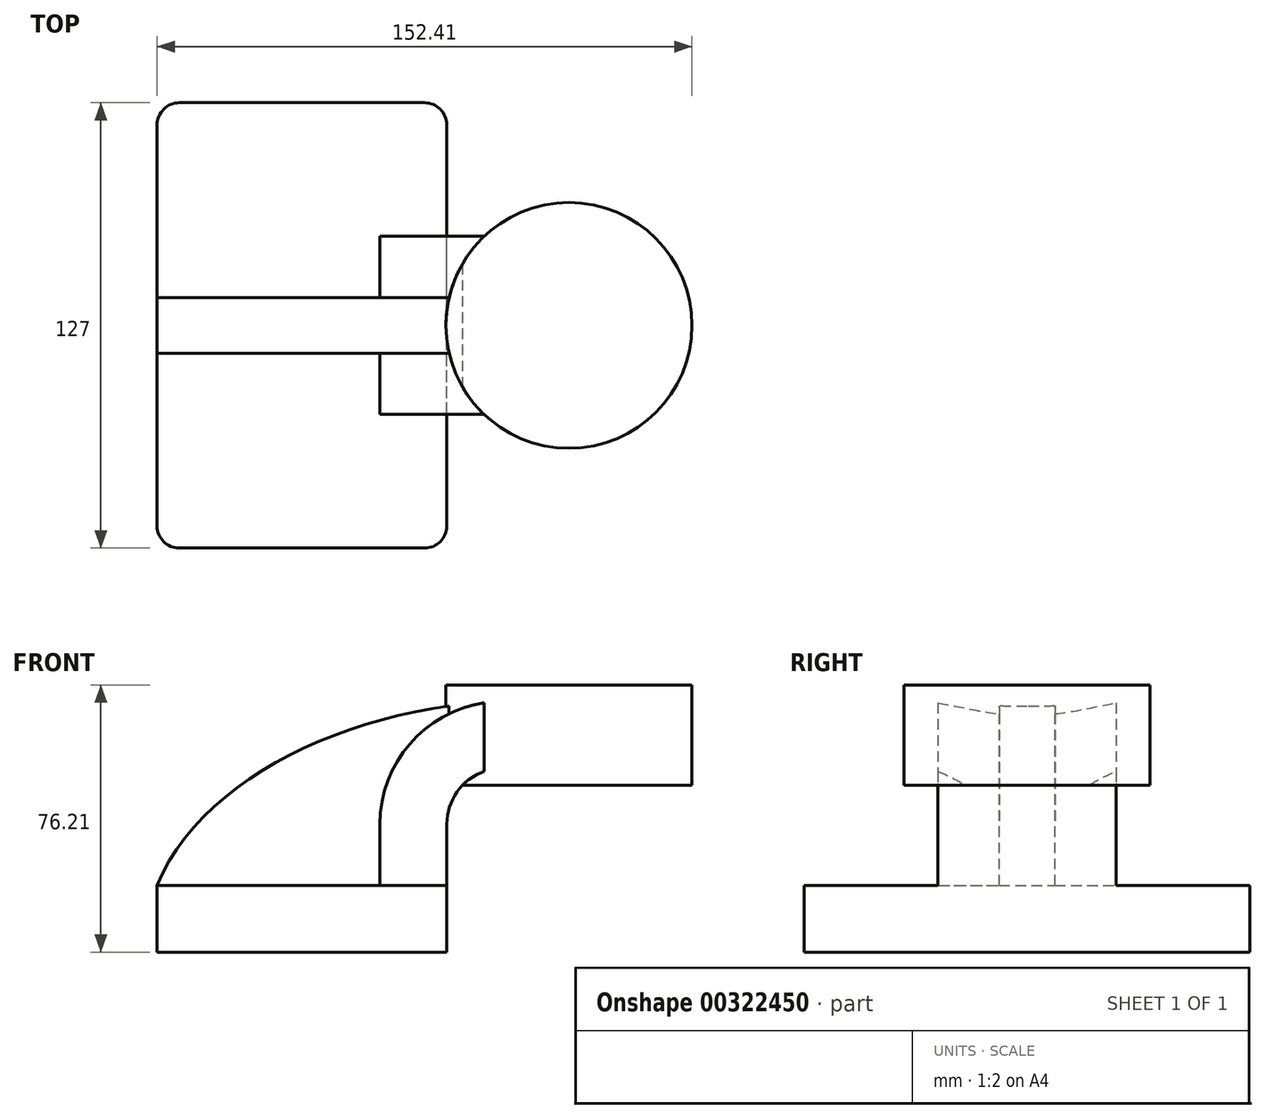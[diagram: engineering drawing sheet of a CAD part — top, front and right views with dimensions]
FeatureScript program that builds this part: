
annotation { "Feature Type Name" : "Feature", "Feature Type Description" : "" }
export const myFeature = defineFeature(function(context is Context, id is Id, definition is map)
    precondition{}
    {
        {
            var Q0;
            Q0=qCreatedBy(makeId("Front.planeOp"),FACE);
            var sketch = newSketch(context, id + "F0", { "sketchPlane" : qUnion([Q0])});
            skLineSegment(sketch, "E0.bottom", {"start": v(-41.28, -9.52) * mm, "end": v(41.28, -9.52) * mm});
            skLineSegment(sketch, "E0.top", {"start": v(-41.28, 9.53) * mm, "end": v(41.28, 9.53) * mm});
            skLineSegment(sketch, "E0.left", {"start": v(-41.27, -9.52) * mm, "end": v(-41.28, 9.53) * mm});
            skLineSegment(sketch, "E0.right", {"start": v(41.28, -9.52) * mm, "end": v(41.28, 9.53) * mm});
            skPoint(sketch, "E0.middle", {"position": v(0, 0) * mm});
            skLineSegment(sketch, "E1.bottom", {"start": v(60.33, 38.1) * mm, "end": v(111.12, 38.1) * mm});
            skLineSegment(sketch, "E1.top", {"start": v(60.32, 66.68) * mm, "end": v(111.12, 66.68) * mm});
            skLineSegment(sketch, "E1.left", {"start": v(60.32, 38.1) * mm, "end": v(60.32, 66.68) * mm});
            skLineSegment(sketch, "E1.right", {"start": v(111.12, 38.1) * mm, "end": v(111.12, 66.68) * mm});
            skPoint(sketch, "E1.middle", {"position": v(85.72, 52.39) * mm});
            skLineSegment(sketch, "E2", {"start": v(41.27, 9.53) * mm, "end": v(41.27, 27) * mm});
            skArc(sketch, "E3", {"start": v(41.27, 27) * mm, "mid": v(45.92, 38.23) * mm, "end": v(57.15, 42.88) * mm});
            skLineSegment(sketch, "E4", {"start": v(57.15, 42.88) * mm, "end": v(76.07, 42.88) * mm});
            skLineSegment(sketch, "E5.0", {"start": v(57.15, 61.93) * mm, "end": v(76.07, 61.93) * mm});
            skArc(sketch, "E5.1", {"start": v(22.22, 27) * mm, "mid": v(32.45, 51.7) * mm, "end": v(57.15, 61.93) * mm});
            skLineSegment(sketch, "E5.2", {"start": v(22.23, 9.53) * mm, "end": v(22.23, 27) * mm});
            skLineSegment(sketch, "E6", {"start": v(22.23, 9.53) * mm, "end": v(41.28, 9.53) * mm});
            skLineSegment(sketch, "E7", {"start": v(76.07, 42.88) * mm, "end": v(76.07, 61.93) * mm});
            skLineSegment(sketch, "E8", {"start": v(41.28, 9.53) * mm, "end": v(22.23, 9.53) * mm});
            skLineSegment(sketch, "E9", {"start": v(76.07, 38.1) * mm, "end": v(76.07, 66.68) * mm});
            skFitSpline(sketch, "E10", {"points": [v(-41.28, 9.53) * mm, v(57.15, 61.93) * mm], "startDerivative": vector(38.05, 92.8) * mm, "endDerivative": vector(127.6, 4.36) * mm});
            skSolve(sketch);
        }
        {
            var Q0;
            Q0=makeQuery(id+"F0.imprint","IMPRINT",FACE,{"disambiguationData":[TD([[makeQuery(id+"F0.imprint","IMPRINT",EDGE,{"derivedFrom":sQuery(id+"F0.wireOp",EDGE,"E0.bottom")}),1.0]])]});
            extrude(context, id + "F1", {"entities" : qUnion([Q0]), "endBound" : BoundingType.SYMMETRIC, "depth" : 127 * mm});
        }
        {
            var Q0;
            {var subQ0=sQuery(id+"F0.wireOp",EDGE,"E4");var subQ1=sQuery(id+"F0.wireOp",EDGE,"E1.left");var subQ2=makeQuery(id+"F0.imprint","INTERSECT",VERTEX,{"derivedFrom":[subQ1,subQ0]});Q0=makeQuery(id+"F0.imprint","IMPRINT",FACE,{"disambiguationData":[TD([[makeQuery(id+"F0.imprint","IMPRINT",EDGE,{"disambiguationData":[TD([[subQ2,-1.0]])],"derivedFrom":subQ1}),-1.0]])]});}
            var Q1;
            Q1=makeQuery(id+"F0.imprint","IMPRINT",FACE,{"disambiguationData":[TD([[makeQuery(id+"F0.imprint","IMPRINT",EDGE,{"derivedFrom":sQuery(id+"F0.wireOp",EDGE,"E2")}),1.0]])]});
            extrude(context, id + "F2", {"entities" : qUnion([Q0, Q1]), "operationType" : NewBodyOperationType.ADD, "endBound" : BoundingType.SYMMETRIC, "depth" : 50.8 * mm});
        }
        {
            var Q0;
            {var subQ0=sQuery(id+"F0.wireOp",EDGE,"E0.top");Q0=makeQuery(id+"F0.imprint","IMPRINT",FACE,{"disambiguationData":[TD([[makeQuery(id+"F0.imprint","IMPRINT",EDGE,{"derivedFrom":subQ0}),1.0]])]});}
            extrude(context, id + "F3", {"entities" : qUnion([Q0]), "operationType" : NewBodyOperationType.ADD, "endBound" : BoundingType.SYMMETRIC, "depth" : 15.88 * mm});
        }
        {
            var Q0;
            {var subQ0=sQuery(id+"F0.wireOp",EDGE,"E1.right");Q0=makeQuery(id+"F0.imprint","IMPRINT",FACE,{"disambiguationData":[TD([[makeQuery(id+"F0.imprint","IMPRINT",EDGE,{"derivedFrom":subQ0}),1.0]])]});}
            var Q1;
            Q1=sQuery(id+"F0.wireOp",EDGE,"E7");
            revolve(context, id + "F4", {"operationType" : NewBodyOperationType.ADD, "entities" : qUnion([Q0]), "axis" : qUnion([Q1]), "revolveType" : RevolveType.FULL});
        }
        {
            var Q0;
            Q0=makeQuery(id+"F1.opExtrude","CAP_EDGE",EDGE,{"disambiguationData":[OSD([sQuery(id+"F0.wireOp",EDGE,"E0.right")])],"isStart":false});
            var Q1;
            Q1=makeQuery(id+"F1.opExtrude","CAP_EDGE",EDGE,{"disambiguationData":[OSD([sQuery(id+"F0.wireOp",EDGE,"E0.left")])],"isStart":false});
            var Q2;
            Q2=makeQuery(id+"F1.opExtrude","CAP_EDGE",EDGE,{"disambiguationData":[OSD([sQuery(id+"F0.wireOp",EDGE,"E0.left")])],"isStart":true});
            var Q3;
            Q3=makeQuery(id+"F1.opExtrude","CAP_EDGE",EDGE,{"disambiguationData":[OSD([sQuery(id+"F0.wireOp",EDGE,"E0.right")])],"isStart":true});
            fillet(context, id + "F5", {"entities" : qUnion([Q0, Q1, Q2, Q3]), "radius" : 6.35 * mm, "tangentPropagation" : true, "allowEdgeOverflow" : false});
        }
    });
